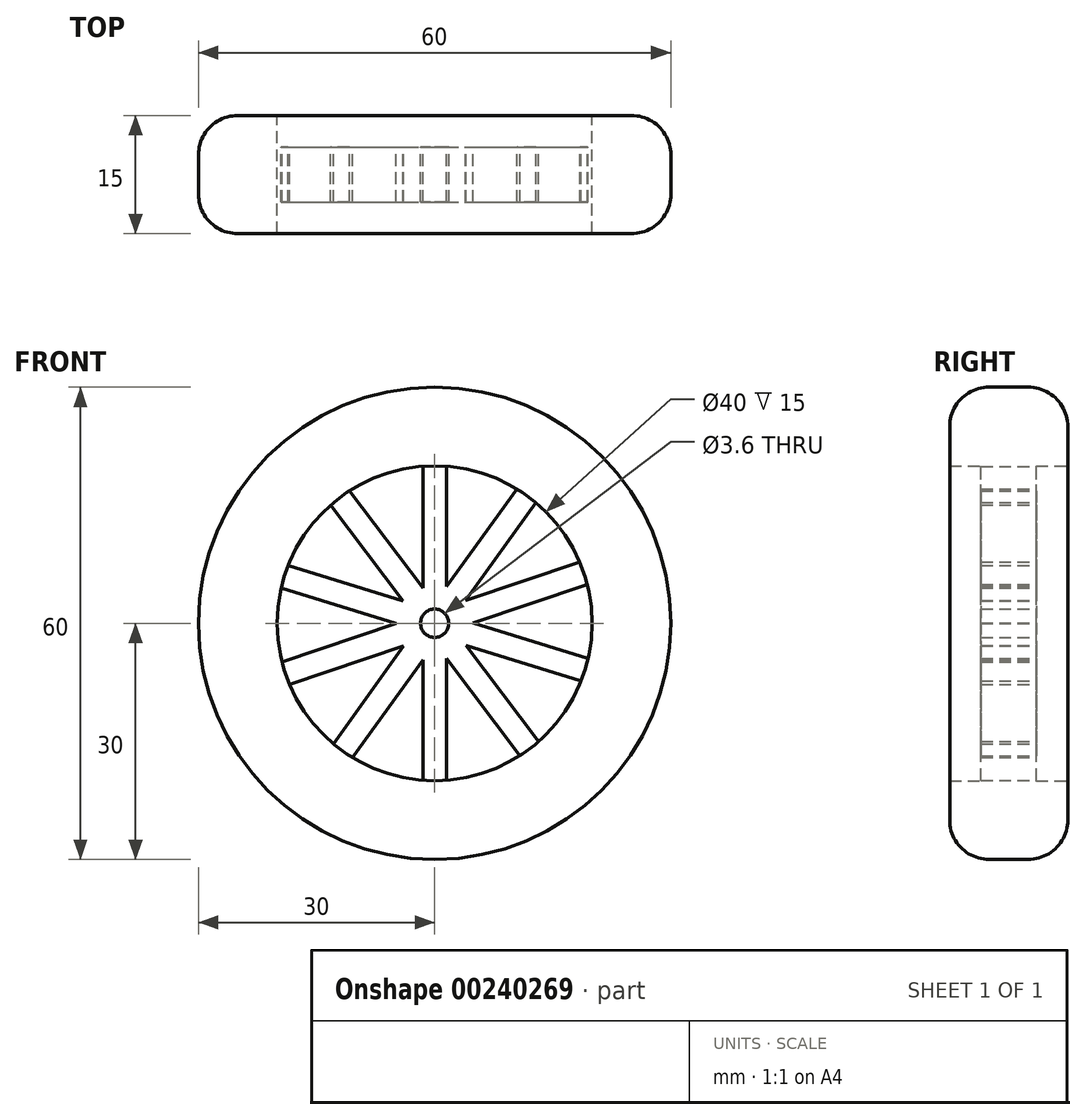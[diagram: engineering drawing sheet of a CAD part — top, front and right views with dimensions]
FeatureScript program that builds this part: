
annotation { "Feature Type Name" : "Feature", "Feature Type Description" : "" }
export const myFeature = defineFeature(function(context is Context, id is Id, definition is map)
    precondition{}
    {
        {
            var Q0;
            Q0=qCreatedBy(makeId("Front.planeOp"),FACE);
            var sketch = newSketch(context, id + "F0", { "sketchPlane" : qUnion([Q0])});
            skCircle(sketch, "E0", {"center": v(0, 0) * mm, "radius": 30 * mm});
            skCircle(sketch, "E1.0", {"center": v(0, 0) * mm, "radius": 20 * mm});
            skSolve(sketch);
        }
        {
            var Q0;
            Q0=qCreatedBy(makeId("Front.planeOp"),FACE);
            var sketch = newSketch(context, id + "F1", { "sketchPlane" : qUnion([Q0])});
            skLineSegment(sketch, "E2.bottom", {"start": v(1.5, -23.26) * mm, "end": v(-1.5, -23.26) * mm});
            skLineSegment(sketch, "E2.top", {"start": v(1.5, 23.26) * mm, "end": v(-1.5, 23.26) * mm});
            skLineSegment(sketch, "E2.left", {"start": v(1.5, -23.26) * mm, "end": v(1.5, 23.26) * mm});
            skLineSegment(sketch, "E2.right", {"start": v(-1.5, -23.26) * mm, "end": v(-1.5, 23.26) * mm});
            skPoint(sketch, "E2.middle", {"position": v(0, 0) * mm});
            skLineSegment(sketch, "E3.1.0", {"start": v(14.8, 18) * mm, "end": v(12.37, 19.76) * mm});
            skLineSegment(sketch, "E3.1.1", {"start": v(-14.8, -18) * mm, "end": v(12.37, 19.76) * mm});
            skLineSegment(sketch, "E3.1.2", {"start": v(-12.37, -19.76) * mm, "end": v(14.8, 18) * mm});
            skLineSegment(sketch, "E3.1.3", {"start": v(-12.37, -19.76) * mm, "end": v(-14.8, -18) * mm});
            skLineSegment(sketch, "E3.2.0", {"start": v(22.53, 5.96) * mm, "end": v(21.58, 8.8) * mm});
            skLineSegment(sketch, "E3.2.1", {"start": v(-22.53, -5.96) * mm, "end": v(21.58, 8.8) * mm});
            skLineSegment(sketch, "E3.2.2", {"start": v(-21.58, -8.8) * mm, "end": v(22.53, 5.96) * mm});
            skLineSegment(sketch, "E3.2.3", {"start": v(-21.58, -8.8) * mm, "end": v(-22.53, -5.96) * mm});
            skLineSegment(sketch, "E3.3.0", {"start": v(21.77, -8.33) * mm, "end": v(22.66, -5.46) * mm});
            skLineSegment(sketch, "E3.3.1", {"start": v(-21.77, 8.33) * mm, "end": v(22.66, -5.46) * mm});
            skLineSegment(sketch, "E3.3.2", {"start": v(-22.66, 5.46) * mm, "end": v(21.77, -8.33) * mm});
            skLineSegment(sketch, "E3.3.3", {"start": v(-22.66, 5.46) * mm, "end": v(-21.77, 8.33) * mm});
            skLineSegment(sketch, "E3.4.0", {"start": v(12.8, -19.48) * mm, "end": v(15.2, -17.67) * mm});
            skLineSegment(sketch, "E3.4.1", {"start": v(-12.8, 19.48) * mm, "end": v(15.2, -17.67) * mm});
            skLineSegment(sketch, "E3.4.2", {"start": v(-15.2, 17.67) * mm, "end": v(12.8, -19.48) * mm});
            skLineSegment(sketch, "E3.4.3", {"start": v(-15.2, 17.67) * mm, "end": v(-12.8, 19.48) * mm});
            skLineSegment(sketch, "E3.anchor1", {"start": v(0, 0) * mm, "end": v(-1.5, 23.26) * mm, "construction": true});
            skLineSegment(sketch, "E3.anchor2", {"start": v(0, 0) * mm, "end": v(15.2, -17.67) * mm, "construction": true});
            skSolve(sketch);
        }
        {
            var Q0;
            Q0 = qSketchRegion(id + "F1", true);
            extrude(context, id + "F2", {"entities" : qUnion([Q0]), "endBound" : BoundingType.SYMMETRIC, "depth" : 7 * mm});
        }
        {
            var Q0;
            Q0 = qSketchRegion(id + "F0", true);
            extrude(context, id + "F3", {"entities" : qUnion([Q0]), "operationType" : NewBodyOperationType.ADD, "endBound" : BoundingType.SYMMETRIC, "depth" : 15 * mm});
        }
        {
            var Q0;
            Q0=qCreatedBy(makeId("Front.planeOp"),FACE);
            var sketch = newSketch(context, id + "F4", { "sketchPlane" : qUnion([Q0])});
            skCircle(sketch, "E4", {"center": v(0, 0) * mm, "radius": 1.8 * mm});
            skCircle(sketch, "E5.0", {"center": v(0, 0) * mm, "radius": 4 * mm});
            skSolve(sketch);
        }
        {
            var Q0;
            Q0 = qSketchRegion(id + "F4", true);
            extrude(context, id + "F5", {"entities" : qUnion([Q0]), "operationType" : NewBodyOperationType.ADD, "endBound" : BoundingType.SYMMETRIC, "depth" : 7 * mm});
        }
        {
            var Q0;
            Q0=makeQuery(id+"F3.opExtrude","CAP_EDGE",EDGE,{"disambiguationData":[OSD([sQuery(id+"F0.wireOp",EDGE,"E0")])],"isStart":false});
            fillet(context, id + "F6", {"entities" : qUnion([Q0]), "radius" : 5 * mm, "tangentPropagation" : true, "allowEdgeOverflow" : false});
        }
        {
            var Q0;
            Q0=makeQuery(id+"F3.opExtrude","CAP_EDGE",EDGE,{"disambiguationData":[OSD([sQuery(id+"F0.wireOp",EDGE,"E0")])],"isStart":true});
            fillet(context, id + "F7", {"entities" : qUnion([Q0]), "radius" : 5 * mm, "tangentPropagation" : true, "allowEdgeOverflow" : false});
        }
    });
